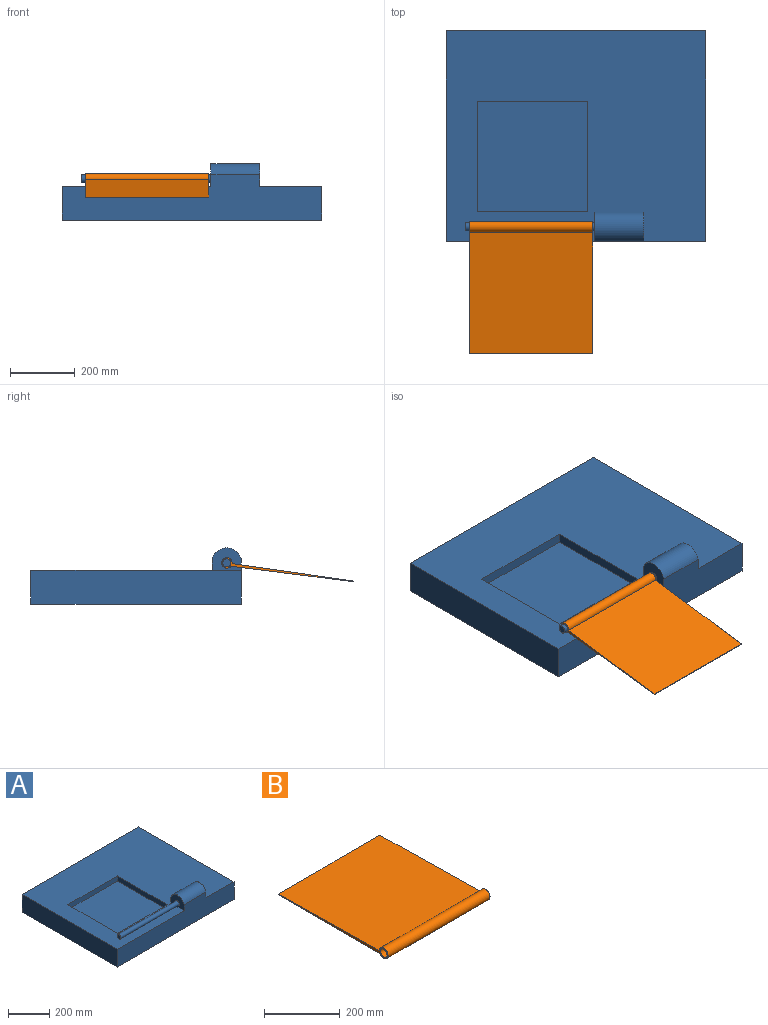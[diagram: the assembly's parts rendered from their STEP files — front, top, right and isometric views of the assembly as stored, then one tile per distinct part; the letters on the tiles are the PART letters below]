
ASSEMBLY  parts=2 mates=1
PART A: 17 faces, bbox 800x650x174.2 mm
  f0: plane 800x650mm, normal (0,0,1), area 390900mm2, adj f1,f2,f3,f4,f5,f7,f8,f10
  f1: plane 800x140mm, normal (0,-1,0), area 89250mm2, adj f0,f2,f3,f4,f6,f7,f9
  f2: plane 90x69.23mm, normal (-1,0,0), area 4933.8mm2, adj f0,f1,f8,f9,f15
  f3: plane 650x105mm, normal (-1,0,0), area 68250mm2, adj f0,f1,f5,f6
  f4: plane 650x105mm, normal (1,0,0), area 68250mm2, adj f0,f1,f5,f6
  f5: plane 800x105mm, normal (0,1,0), area 84000mm2, adj f0,f3,f4,f6
  f6: plane 800x650mm, normal (0,0,-1), area 520000mm2, adj f1,f3,f4,f5
  f7: plane 90x69.23mm, normal (1,0,0), area 5424.7mm2, adj f0,f1,f8,f9
  f8: plane 150x35mm, normal (0,1,0), area 5250mm2, adj f0,f2,f7,f9
  f9: cylinder r=46.7mm len=150mm, axis (1,0,0), area 18218.4mm2, adj f1,f2,f7,f8
  f10: plane 340x30mm, normal (1,0,0), area 10200mm2, adj f0,f11,f13,f14
  f11: plane 340x30mm, normal (0,1,0), area 10200mm2, adj f0,f10,f12,f14
  f12: plane 340x30mm, normal (-1,0,0), area 10200mm2, adj f0,f11,f13,f14
  f13: plane 340x30mm, normal (0,-1,0), area 10200mm2, adj f0,f10,f12,f14
  f14: plane 340x340mm, normal (0,0,1), area 115600mm2, adj f10,f11,f12,f13
  f15: cylinder r=12.5mm len=400mm, axis (1,0,0), area 31415.9mm2, adj f2,f16
  f16: plane 25x25mm, normal (-1,0,0), area 490.9mm2, adj f15
PART B: 7 faces, bbox 380x410.2x32.5 mm
  f0: plane 410.23x32.47mm, normal (-1,0,0), area 2232.2mm2, adj f1,f3,f4,f5,f6
  f1: plane 380x2.04mm, normal (0,1,0), area 774.1mm2, adj f0,f2,f3,f4
  f2: plane 410.23x32.47mm, normal (1,0,0), area 2232.2mm2, adj f1,f3,f4,f5,f6
  f3: plane 380x380mm, normal (0,0,-1), area 144400mm2, adj f0,f1,f2,f5
  f4: plane 380x377.77mm, normal (0,0.02,1), area 143569.2mm2, adj f0,f1,f2,f5
  f5: cylinder r=16.23mm len=380mm, axis (-1,0,0), area 35580mm2, adj f0,f2,f3,f4
  f6: cylinder r=12.5mm len=380mm, axis (-1,0,0), area 29845.1mm2, adj f0,f2
PLACE A t=(-149.69,160.07,304.08)mm
PLACE B rot(axis=(0,-0.06,1),180deg) t=(-364.86,-348.36,406.55)mm
MATE cylindrical B.f5 <-> A.f9  axis (1,0,0) through (-536.43,-217.05,431.61)mm
